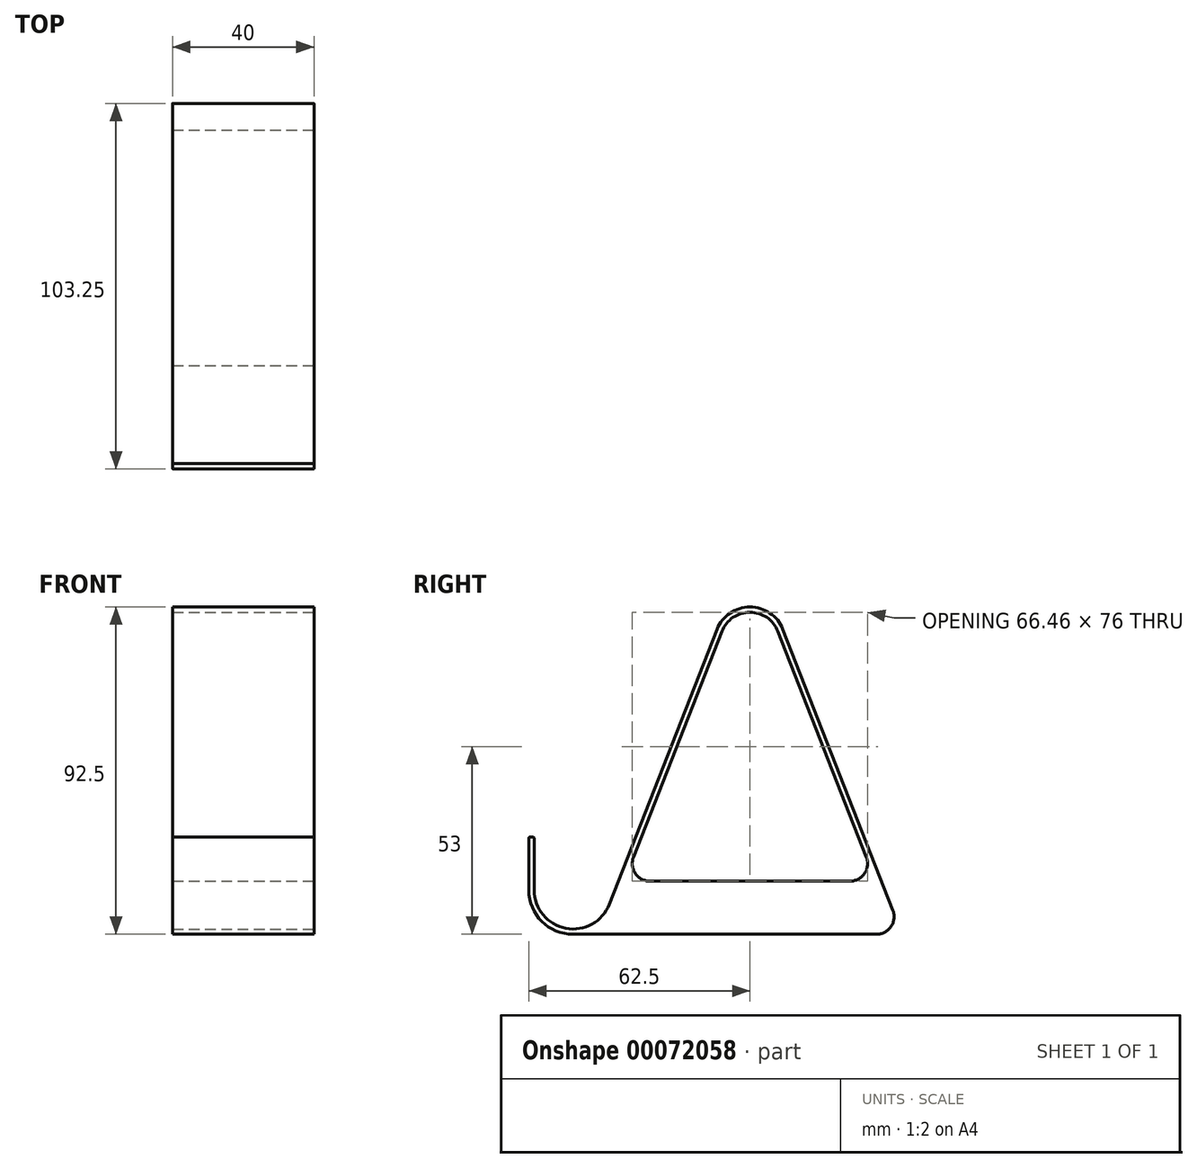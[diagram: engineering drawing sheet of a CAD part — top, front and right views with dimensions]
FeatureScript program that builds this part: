
annotation { "Feature Type Name" : "Feature", "Feature Type Description" : "" }
export const myFeature = defineFeature(function(context is Context, id is Id, definition is map)
    precondition{}
    {
        {
            var Q0;
            Q0=qCreatedBy(makeId("Right.planeOp"),FACE);
            var sketch = newSketch(context, id + "F0", { "sketchPlane" : qUnion([Q0])});
            skArc(sketch, "E0", {"start": v(-12.5, 0) * mm, "mid": v(-8.84, -8.84) * mm, "end": v(0, -12.5) * mm});
            skArc(sketch, "E1", {"start": v(57.91, 73.1) * mm, "mid": v(50, 78.5) * mm, "end": v(42.09, 73.1) * mm});
            skLineSegment(sketch, "E2", {"start": v(17.08, 9.33) * mm, "end": v(42.09, 73.1) * mm});
            skLineSegment(sketch, "E3", {"start": v(50, 70) * mm, "end": v(50, -60.4) * mm, "construction": true});
            skLineSegment(sketch, "E4", {"start": v(-12.5, 0) * mm, "end": v(-12.5, 14.6) * mm});
            skLineSegment(sketch, "E5.0", {"start": v(-11, 0) * mm, "end": v(-11, 14.6) * mm});
            skLineSegment(sketch, "E5.1", {"start": v(90.4, -5.67) * mm, "end": v(59.31, 73.65) * mm});
            skArc(sketch, "E5.2", {"start": v(59.31, 73.65) * mm, "mid": v(50, 80) * mm, "end": v(40.69, 73.65) * mm});
            skLineSegment(sketch, "E5.3", {"start": v(10.24, -4.02) * mm, "end": v(40.69, 73.65) * mm});
            skArc(sketch, "E5.4", {"start": v(-11, 0) * mm, "mid": v(-2.04, -10.8) * mm, "end": v(10.24, -4.02) * mm});
            skLineSegment(sketch, "E6", {"start": v(-12.1, 15) * mm, "end": v(-11.4, 15) * mm});
            skPoint(sketch, "E7.visualSharp", {"position": v(-12.5, 15) * mm});
            skArc(sketch, "E7.filletArc", {"start": v(-12.1, 15) * mm, "mid": v(-12.38, 14.88) * mm, "end": v(-12.5, 14.6) * mm});
            skPoint(sketch, "E8.visualSharp", {"position": v(-11, 15) * mm});
            skArc(sketch, "E8.filletArc", {"start": v(-11, 14.6) * mm, "mid": v(-11.12, 14.88) * mm, "end": v(-11.4, 15) * mm});
            skLineSegment(sketch, "E9", {"start": v(0, -12.5) * mm, "end": v(85.75, -12.5) * mm});
            skLineSegment(sketch, "E10.0", {"start": v(21.74, 2.5) * mm, "end": v(78.26, 2.5) * mm});
            skLineSegment(sketch, "E11.trimOffspring", {"start": v(82.92, 9.33) * mm, "end": v(57.91, 73.1) * mm});
            skPoint(sketch, "E12.orphan", {"position": v(11.64, -4.56) * mm});
            skPoint(sketch, "E13.visualSharp", {"position": v(14.4, 2.5) * mm});
            skArc(sketch, "E13.filletArc", {"start": v(17.08, 9.33) * mm, "mid": v(17.6, 4.68) * mm, "end": v(21.74, 2.5) * mm});
            skPoint(sketch, "E14.visualSharp", {"position": v(85.6, 2.5) * mm});
            skArc(sketch, "E14.filletArc", {"start": v(78.26, 2.5) * mm, "mid": v(82.4, 4.68) * mm, "end": v(82.92, 9.33) * mm});
            skArc(sketch, "E15.filletArc", {"start": v(85.75, -12.5) * mm, "mid": v(89.89, -10.32) * mm, "end": v(90.4, -5.67) * mm});
            skSolve(sketch);
        }
        {
            var Q0;
            Q0=makeQuery(id+"F0.imprint","IMPRINT",FACE,{"disambiguationData":[TD([[makeQuery(id+"F0.imprint","IMPRINT",EDGE,{"derivedFrom":sQuery(id+"F0.wireOp",EDGE,"E0")}),1.0]])]});
            extrude(context, id + "F1", {"entities" : qUnion([Q0]), "oppositeDirection" : true, "depth" : 40 * mm});
        }
    });
